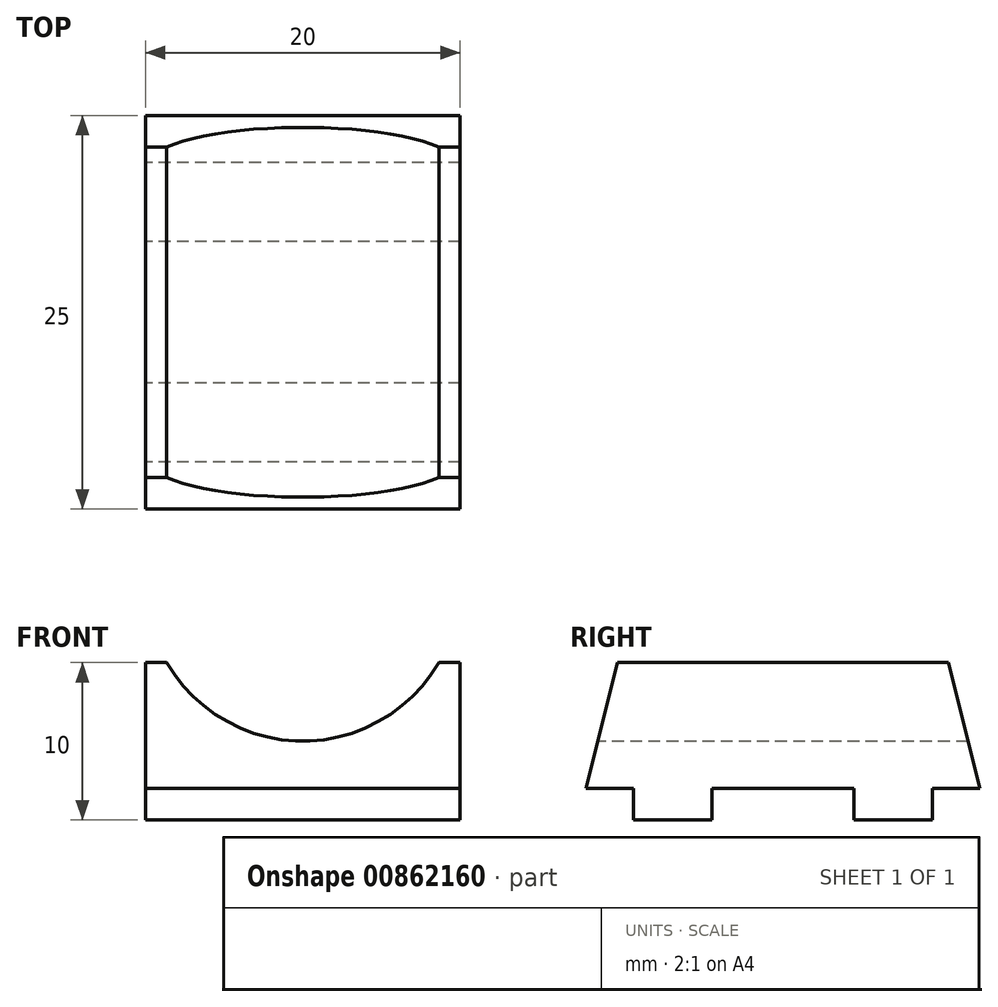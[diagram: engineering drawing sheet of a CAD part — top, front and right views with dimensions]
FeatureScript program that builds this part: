
annotation { "Feature Type Name" : "Feature", "Feature Type Description" : "" }
export const myFeature = defineFeature(function(context is Context, id is Id, definition is map)
    precondition{}
    {
        {
            var Q0;
            Q0=qCreatedBy(makeId("Right.planeOp"),FACE);
            var sketch = newSketch(context, id + "F0", { "sketchPlane" : qUnion([Q0])});
            skLineSegment(sketch, "E0", {"start": v(0, 0) * mm, "end": v(25, 0) * mm});
            skLineSegment(sketch, "E1", {"start": v(25, 0) * mm, "end": v(23, 8) * mm});
            skLineSegment(sketch, "E2", {"start": v(23, 8) * mm, "end": v(2, 8) * mm});
            skLineSegment(sketch, "E3", {"start": v(2, 8) * mm, "end": v(0, 0) * mm});
            skLineSegment(sketch, "E4", {"start": v(25, 0) * mm, "end": v(22, 0) * mm});
            skLineSegment(sketch, "E5", {"start": v(22, 0) * mm, "end": v(22, -2) * mm});
            skLineSegment(sketch, "E6", {"start": v(22, -2) * mm, "end": v(17, -2) * mm});
            skLineSegment(sketch, "E7", {"start": v(17, -2) * mm, "end": v(17, 0) * mm});
            skLineSegment(sketch, "E8", {"start": v(17, 0) * mm, "end": v(8, 0) * mm});
            skLineSegment(sketch, "E9", {"start": v(8, 0) * mm, "end": v(8, -2) * mm});
            skLineSegment(sketch, "E10", {"start": v(8, -2) * mm, "end": v(3, -2) * mm});
            skLineSegment(sketch, "E11", {"start": v(3, -2) * mm, "end": v(3, 0) * mm});
            skLineSegment(sketch, "E12", {"start": v(3, 0) * mm, "end": v(0, 0) * mm});
            skSolve(sketch);
        }
        {
            var Q0;
            Q0 = qSketchRegion(id + "F0", true);
            extrude(context, id + "F1", {"entities" : qUnion([Q0]), "depth" : 20 * mm, "offsetDistance" : 25.4 * mm});
        }
        {
            var Q0;
            Q0=qCreatedBy(makeId("Front.planeOp"),FACE);
            var sketch = newSketch(context, id + "F2", { "sketchPlane" : qUnion([Q0])});
            skCircle(sketch, "E13", {"center": v(10, 13) * mm, "radius": 10 * mm});
            skSolve(sketch);
        }
        {
            var Q0;
            Q0=makeQuery(id+"F2.imprint","IMPRINT",FACE,{"disambiguationData":[TD([[makeQuery(id+"F2.imprint","IMPRINT",EDGE,{"derivedFrom":sQuery(id+"F2.wireOp",EDGE,"E13")}),1.0]])]});
            extrude(context, id + "F3", {"entities" : qUnion([Q0]), "operationType" : NewBodyOperationType.REMOVE, "oppositeDirection" : true, "depth" : 25.4 * mm, "offsetDistance" : 25.4 * mm});
        }
    });
